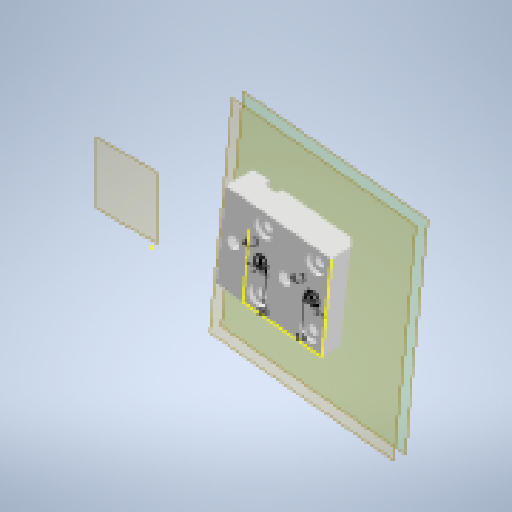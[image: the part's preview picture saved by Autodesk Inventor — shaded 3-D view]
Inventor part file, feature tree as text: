
AUTODESK INVENTOR PART (.ipt)
format: ipt  version: 2024.2 (Build 282272000, 272)  size: 332,800 bytes
history: native  units: mm
features: other x7, sketch x7, extrude x6, chamfer x1, projected_geometry x1
ambient origin geometry x8: Origin, YZ Plane, XZ Plane, XY Plane, X Axis, Y Axis, Z Axis, Center Point
bodies: Body1 (feature_tree)
feature tree (22):
  other  "Твердое тело1"
  other  "РабПлоскость1"
  other  "РабПлоскость2"
  extrude  "Выдавливание1"  Depth=5.0mm
  sketch  "Эскиз3"
  other  "РабПлоскость3"
  extrude  "Выдавливание3"  Depth=5.0mm
  extrude  "Выдавливание4"  Depth=5.0mm
  sketch  "Эскиз6"
  extrude  "Выдавливание5"  Depth=5.0mm
  extrude  "Выдавливание6"  Depth=4.3mm
  chamfer  "Фаска1"  Distance=4.3mm
  extrude  "Выдавливание7"  Depth=16.0mm
  sketch  "Эскиз2"
  sketch  "Эскиз4"
  sketch  "Эскиз5"
  projected_geometry  "Спроецированная петля1"
  sketch  "Эскиз7"
  sketch  "Эскиз8"
  other  "<userpath>\Documents\Artist\3D\каретка.iam"
  other  "каретка.iam"
  other  "ANY:5"
